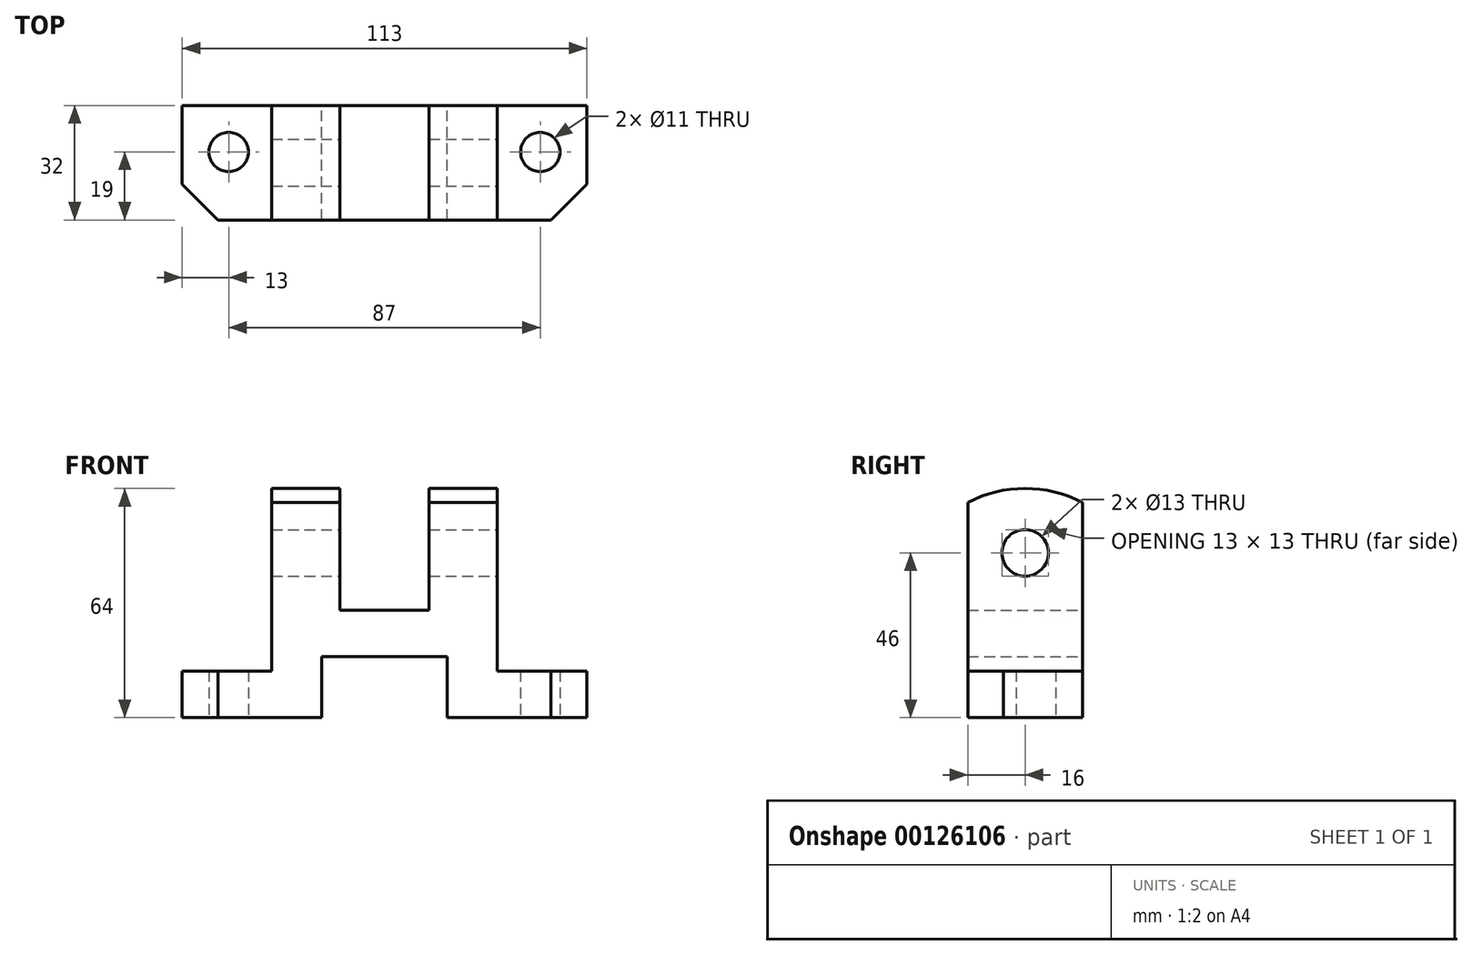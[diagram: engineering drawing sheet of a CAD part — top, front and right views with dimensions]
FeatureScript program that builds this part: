
annotation { "Feature Type Name" : "Feature", "Feature Type Description" : "" }
export const myFeature = defineFeature(function(context is Context, id is Id, definition is map)
    precondition{}
    {
        {
            var Q0;
            Q0=qCreatedBy(makeId("Front.planeOp"),FACE);
            var sketch = newSketch(context, id + "F0", { "sketchPlane" : qUnion([Q0])});
            skLineSegment(sketch, "E0", {"start": v(-56.5, 0) * mm, "end": v(-56.5, 13) * mm});
            skLineSegment(sketch, "E1", {"start": v(-56.5, 13) * mm, "end": v(-31.5, 13) * mm});
            skLineSegment(sketch, "E2", {"start": v(-31.5, 13) * mm, "end": v(-31.5, 64) * mm});
            skLineSegment(sketch, "E3", {"start": v(-31.5, 64) * mm, "end": v(-12.5, 64) * mm});
            skLineSegment(sketch, "E4", {"start": v(-12.5, 64) * mm, "end": v(-12.5, 30) * mm});
            skLineSegment(sketch, "E5", {"start": v(-12.5, 30) * mm, "end": v(12.5, 30) * mm});
            skLineSegment(sketch, "E6", {"start": v(12.5, 30) * mm, "end": v(12.5, 64) * mm});
            skLineSegment(sketch, "E7", {"start": v(12.5, 64) * mm, "end": v(31.5, 64) * mm});
            skLineSegment(sketch, "E8", {"start": v(31.5, 64) * mm, "end": v(31.5, 13) * mm});
            skLineSegment(sketch, "E9", {"start": v(31.5, 13) * mm, "end": v(56.5, 13) * mm});
            skLineSegment(sketch, "E10", {"start": v(56.5, 13) * mm, "end": v(56.5, 0) * mm});
            skLineSegment(sketch, "E11", {"start": v(56.5, 0) * mm, "end": v(17.5, 0) * mm});
            skLineSegment(sketch, "E12", {"start": v(17.5, 0) * mm, "end": v(17.5, 17) * mm});
            skLineSegment(sketch, "E13", {"start": v(17.5, 17) * mm, "end": v(-17.5, 17) * mm});
            skLineSegment(sketch, "E14", {"start": v(-17.5, 17) * mm, "end": v(-17.5, 0) * mm});
            skLineSegment(sketch, "E15", {"start": v(-17.5, 0) * mm, "end": v(-56.5, 0) * mm});
            skSolve(sketch);
        }
        {
            var Q0;
            Q0=makeQuery(id+"F0.imprint","IMPRINT",FACE,{"disambiguationData":[TD([[makeQuery(id+"F0.imprint","IMPRINT",EDGE,{"derivedFrom":sQuery(id+"F0.wireOp",EDGE,"E0")}),-1.0]])]});
            extrude(context, id + "F1", {"entities" : qUnion([Q0]), "endBound" : BoundingType.SYMMETRIC, "depth" : 32 * mm});
        }
        {
            var Q0;
            Q0=qCreatedBy(makeId("Right.planeOp"),FACE);
            var sketch = newSketch(context, id + "F2", { "sketchPlane" : qUnion([Q0])});
            skLineSegment(sketch, "E16.0", {"start": v(-16, 64) * mm, "end": v(16, 64) * mm});
            skLineSegment(sketch, "E17.0", {"start": v(-16, 64) * mm, "end": v(-16, 13) * mm});
            skLineSegment(sketch, "E17.1", {"start": v(16, 64) * mm, "end": v(16, 13) * mm});
            skArc(sketch, "E18", {"start": v(16, 60.13) * mm, "mid": v(0, 64) * mm, "end": v(-16, 60.13) * mm});
            skPoint(sketch, "E19", {"position": v(0, 64) * mm});
            skSolve(sketch);
        }
        {
            var Q0;
            Q0 = qSketchRegion(id + "F2", true);
            extrude(context, id + "F3", {"entities" : qUnion([Q0]), "operationType" : NewBodyOperationType.REMOVE, "endBound" : BoundingType.THROUGH_ALL, "oppositeDirection" : true, "depth" : 25 * mm, "hasSecondDirection" : true, "secondDirectionBound" : SecondDirectionBoundingType.THROUGH_ALL, "secondDirectionOppositeDirection" : false, "secondDirectionDepth" : 25 * mm});
        }
        {
            var Q0;
            Q0=makeQuery(id+"F1.opExtrude","CAP_EDGE",EDGE,{"disambiguationData":[OSD([sQuery(id+"F0.wireOp",EDGE,"E10")])],"isStart":false});
            chamfer(context, id + "F4", {"entities" : qUnion([Q0]), "width" : 10 * mm, "tangentPropagation" : true});
        }
        {
            var Q0;
            Q0=makeQuery(id+"F1.opExtrude","CAP_EDGE",EDGE,{"disambiguationData":[OSD([sQuery(id+"F0.wireOp",EDGE,"E0")])],"isStart":false});
            chamfer(context, id + "F5", {"entities" : qUnion([Q0]), "width" : 10 * mm, "tangentPropagation" : true});
        }
        {
            var Q0;
            Q0=qCreatedBy(makeId("Top.planeOp"),FACE);
            var sketch = newSketch(context, id + "F6", { "sketchPlane" : qUnion([Q0])});
            skCircle(sketch, "E20", {"center": v(-43.5, 3) * mm, "radius": 5.5 * mm});
            skCircle(sketch, "E21", {"center": v(43.5, 3) * mm, "radius": 5.5 * mm});
            skSolve(sketch);
        }
        {
            var Q0;
            Q0 = qSketchRegion(id + "F6", true);
            extrude(context, id + "F7", {"entities" : qUnion([Q0]), "operationType" : NewBodyOperationType.REMOVE, "endBound" : BoundingType.THROUGH_ALL, "depth" : 25 * mm});
        }
        {
            var Q0;
            Q0=makeQuery(id+"F1.opExtrude","SWEPT_FACE",FACE,{"disambiguationData":[OSD([sQuery(id+"F0.wireOp",EDGE,"E8")])]});
            var sketch = newSketch(context, id + "F8", { "sketchPlane" : qUnion([Q0])});
            skLineSegment(sketch, "E22", {"start": v(0, 0) * mm, "end": v(0, 75.36) * mm, "construction": true});
            skPoint(sketch, "E22.endSnap0", {"position": v(0, 64) * mm});
            skCircle(sketch, "E23", {"center": v(0, 46) * mm, "radius": 6.5 * mm});
            skSolve(sketch);
        }
        {
            var Q0;
            Q0 = qSketchRegion(id + "F8", true);
            extrude(context, id + "F9", {"entities" : qUnion([Q0]), "operationType" : NewBodyOperationType.REMOVE, "endBound" : BoundingType.THROUGH_ALL, "oppositeDirection" : true, "depth" : 25 * mm});
        }
    });
